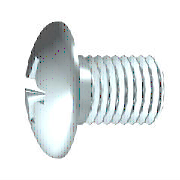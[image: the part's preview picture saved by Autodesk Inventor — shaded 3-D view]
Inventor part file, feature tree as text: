
AUTODESK INVENTOR PART (.ipt)
format: ipt  version: 2014 SP1 (Build 180222100, 222)  size: 268,288 bytes
history: native  units: mm (DEFAULTED — no unit token found)
features: sketch x1, plane x1, extrude x1, other x1
ambient origin geometry x7: Origin, YZ Plane, XZ Plane, X Axis, Y Axis, Z Axis, Center Point
bodies: Solid1 (feature_tree), Body (feature_tree)
feature tree (4):
  sketch  "Sketch1"  dims[d1=2.5146mm d2=1.4986mm d15=90.0deg d3=-1.8034mm d4=45.0deg d5=0.889mm d6=2.667mm d7=0.2413mm d8=11.3771mm d9=0.0mm d12=10.821041mm d13=4.625123mm d16=2.667mm d17=1.3335mm d52=10.0mm d18=0.872665mm d54=90.0deg d19=0.09652mm d20=0.0mm d21=2.5146mm d22=11.3771mm d23=0.529167mm d24=1.8034mm d25=3.18643mm d27=0.254mm d29=4.9022mm d30=12.7mm d72=0.0mm d73=0.0mm d74=0.00254mm]
  plane  "Workplane"
  extrude  "Slot"  Depth=0.00254mm
  other  "Cut"
